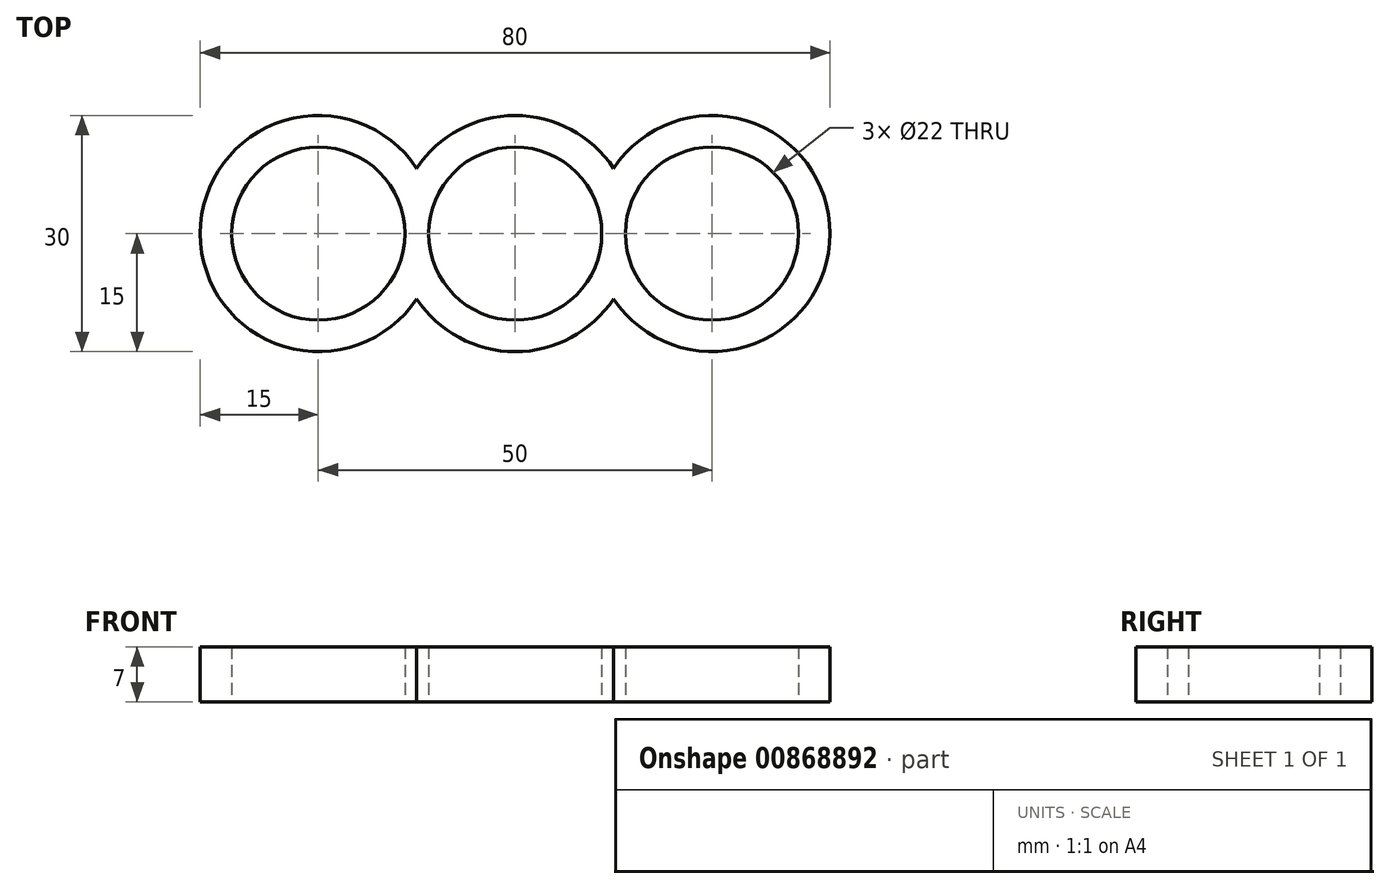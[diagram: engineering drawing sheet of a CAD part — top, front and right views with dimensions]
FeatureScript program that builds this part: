
annotation { "Feature Type Name" : "Feature", "Feature Type Description" : "" }
export const myFeature = defineFeature(function(context is Context, id is Id, definition is map)
    precondition{}
    {
        {
            var Q0;
            Q0=qCreatedBy(makeId("Top.planeOp"),FACE);
            var sketch = newSketch(context, id + "F0", { "sketchPlane" : qUnion([Q0])});
            skArc(sketch, "E0", {"start": v(0, 11) * mm, "mid": v(-11, 0) * mm, "end": v(0, -11) * mm});
            skArc(sketch, "E1", {"start": v(-12.5, -8.3) * mm, "mid": v(-7.1, -13.22) * mm, "end": v(0, -15) * mm});
            skCircle(sketch, "E2", {"center": v(-25, 0) * mm, "radius": 11 * mm});
            skArc(sketch, "E3", {"start": v(-12.5, 8.3) * mm, "mid": v(-40, 0) * mm, "end": v(-12.5, -8.3) * mm});
            skArc(sketch, "E4.trimOffspring", {"start": v(0, 15) * mm, "mid": v(-7.1, 13.22) * mm, "end": v(-12.5, 8.3) * mm});
            skArc(sketch, "E5.MirrorCS", {"start": v(12.5, 8.3) * mm, "mid": v(40, 0) * mm, "end": v(12.5, -8.3) * mm});
            skCircle(sketch, "E6.MirrorC", {"center": v(25, 0) * mm, "radius": 11 * mm});
            skArc(sketch, "E7.MirrorCS", {"start": v(0, 15) * mm, "mid": v(7.1, 13.22) * mm, "end": v(12.5, 8.3) * mm});
            skArc(sketch, "E8.MirrorCS", {"start": v(12.5, -8.3) * mm, "mid": v(7.1, -13.22) * mm, "end": v(0, -15) * mm});
            skArc(sketch, "E9.MirrorCS", {"start": v(0, 11) * mm, "mid": v(11, 0) * mm, "end": v(0, -11) * mm});
            skSolve(sketch);
        }
        {
            var Q0;
            Q0 = qSketchRegion(id + "F0", true);
            extrude(context, id + "F1", {"entities" : qUnion([Q0]), "depth" : 7 * mm, "offsetDistance" : 25.4 * mm});
        }
    });
